# Revit family: Reece_Toilet_Kado_Lux_Pan Wall Hung
name_source: partatom
category: Plumbing Fixtures
revit_build: Autodesk Revit 2018 (Build: 20180329_1100(x64)
units: mm (PartAtom-declared; Revit-internal decimal feet)

## family parameters
Always vertical = Yes
Cut with Voids When Loaded = No
Part Type = Normal
Room Calculation Point = No
Round Connector Dimension = Use Diameter
Shared = No
Work Plane-Based = No

## types (2) — shared parameters
Disclaimer = THIS FILE IS THE PROPERTY OF THE REECE GROUP. IT MAY NOT BE REPRODUCED, REVERSE-ENGINEERED OR MODIFIED. ANY REPUBLICATION, TRANSMISSION OR DISTRIBUTION FOR THE PURPOSE OF COMMERCIALLY EXPLOITING THE FILES IS PROHIBITED.
Manufacturer = Kado
Model = Lux
Reece_Back Distance = 90 mm
Reece_Bottom-Inlet = 30 mm  [stored 0.0984252 ft]
Reece_Detail_Additional = Rimless
Reece_Detail_Connector = P Trap
Reece_Material-Cistern = Reece_Vitreous China_White
Reece_Material-Main = Reece_Vitreous China_White
Reece_Material-Seat = Reece_Acrylic_White
Reece_Material-Secondary = Reece_Brass_Chrome
Reece_Overall-Height = 340 mm  [stored 1.11549 ft]
Reece_Overall-Length = 545 mm  [stored 1.78806 ft]
Reece_Overall-Width = 360 mm  [stored 1.1811 ft]
Reece_P-Trap = 102 mm
Reece_Product-Brand = Kado
Reece_Product-Mount = Wall Hung
Reece_Product-Sub Brand = Lux
Reece_Product-Web Page = https://www.reece.com.au
Reece_Product_Type = Tap
Reece_Seat-Height = 340 mm  [stored 1.11549 ft]
Reece_Seat-Visibility = Yes
Type Comments = Tap
URL = https://www.reece.com.au
zero-valued in all types: Reece_Back-Inlet, Reece_S-Trap

## per-type parameters (varying)
| type | Description | Keynote | Reece_Product-Description | Reece_Product-Number | Reece_Seat-Type |
| Soft Close Quick Release_White | Kado Lux Wall Hung Rimless Pan with Soft Close Quick Release Seat White (4 Star) | Product #9509096, Reece_Toilet_Kado_Lux_Pan Wall Hung - Soft Close Quick Release_White | Kado Lux Wall Hung Rimless Pan with Soft Close Quick Release Seat White (4 Star) | 9509096 | Reece_Seat_Kado Lux_Standard_Nested : Reece_140 Axis Distance 455x360 |
| Soft Close Quick Release Thin_White | Kado Lux Wall Hung Rimless Pan with Thin Soft Close Quick Release Seat White (4 Star) | Product #9509097, Reece_Toilet_Kado_Lux_Pan Wall Hung - Soft Close Quick Release Thin_White | Kado Lux Wall Hung Rimless Pan with Thin Soft Close Quick Release Seat White (4 Star) | 9509097 | Reece_Seat_Kado Lux_Thin_Nested : Reece_140 Axis Distance 455x360 |

note: [stored X ft] marks values corroborated as IEEE doubles in the binary element streams (Revit-internal decimal feet)

## geometry (parser evidence)
native form markers: Sweep x9
no freeform markers — native parametric forms only
